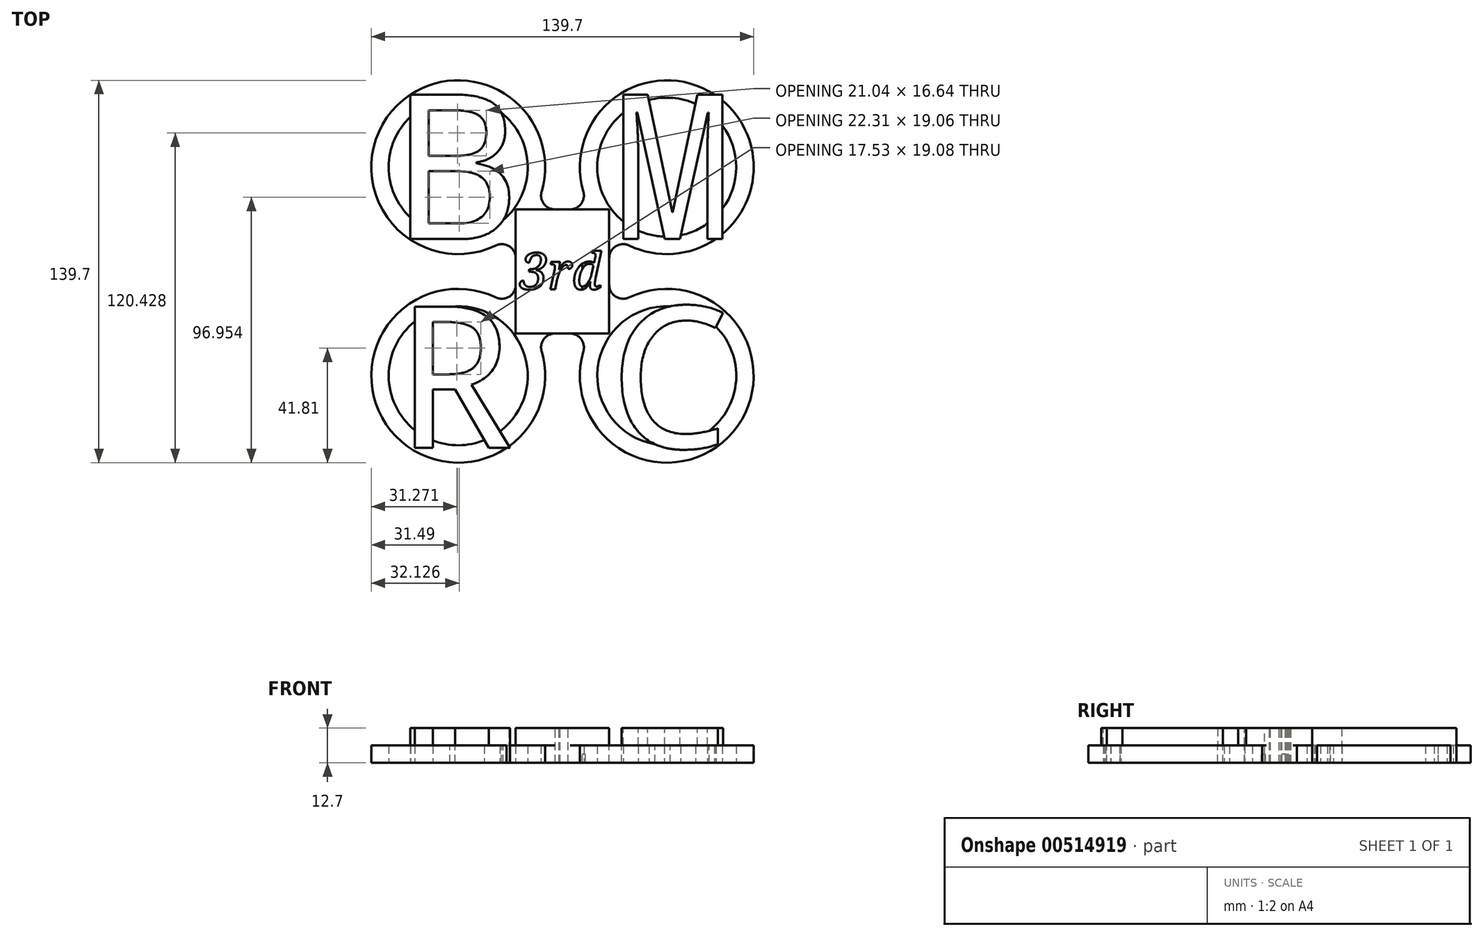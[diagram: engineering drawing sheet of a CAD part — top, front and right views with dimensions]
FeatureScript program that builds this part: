
annotation { "Feature Type Name" : "Feature", "Feature Type Description" : "" }
export const myFeature = defineFeature(function(context is Context, id is Id, definition is map)
    precondition{}
    {
        {
            var Q0;
            Q0=qCreatedBy(makeId("Top.planeOp"),FACE);
            var sketch = newSketch(context, id + "F0", { "sketchPlane" : qUnion([Q0])});
            skLineSegment(sketch, "E0.bottom", {"start": v(38.1, -38.1) * mm, "end": v(-38.1, -38.1) * mm, "construction": true});
            skLineSegment(sketch, "E0.top", {"start": v(38.1, 38.1) * mm, "end": v(-38.1, 38.1) * mm, "construction": true});
            skLineSegment(sketch, "E0.left", {"start": v(38.1, -38.1) * mm, "end": v(38.1, 38.1) * mm, "construction": true});
            skLineSegment(sketch, "E0.right", {"start": v(-38.1, -38.1) * mm, "end": v(-38.1, 38.1) * mm, "construction": true});
            skPoint(sketch, "E0.middle", {"position": v(0, 0) * mm});
            skCircle(sketch, "E1", {"center": v(-38.1, 38.1) * mm, "radius": 31.75 * mm});
            skCircle(sketch, "E2", {"center": v(-38.1, 38.1) * mm, "radius": 25.4 * mm});
            skCircle(sketch, "E3", {"center": v(38.1, 38.1) * mm, "radius": 31.75 * mm});
            skCircle(sketch, "E4", {"center": v(38.1, 38.1) * mm, "radius": 25.4 * mm});
            skCircle(sketch, "E5", {"center": v(-38.1, -38.1) * mm, "radius": 31.75 * mm});
            skCircle(sketch, "E6", {"center": v(-38.1, -38.1) * mm, "radius": 25.4 * mm});
            skCircle(sketch, "E7", {"center": v(38.1, -38.1) * mm, "radius": 31.75 * mm});
            skCircle(sketch, "E8", {"center": v(38.1, -38.1) * mm, "radius": 25.4 * mm});
            skSolve(sketch);
        }
        {
            var Q0;
            Q0=qSketchRegion(id+"F0",true);
            extrude(context, id + "F1", {"entities" : qUnion([Q0]), "depth" : 6.35 * mm, "offsetDistance" : 25.4 * mm});
        }
        {
            var Q0;
            Q0=qCreatedBy(makeId("Top.planeOp"),FACE);
            var sketch = newSketch(context, id + "F2", { "sketchPlane" : qUnion([Q0])});
            skLineSegment(sketch, "E9.bottom", {"start": v(-17.08, -22.68) * mm, "end": v(17.08, -22.68) * mm});
            skLineSegment(sketch, "E9.top", {"start": v(-17.08, 22.68) * mm, "end": v(17.08, 22.68) * mm});
            skLineSegment(sketch, "E9.left", {"start": v(-17.08, -22.68) * mm, "end": v(-17.08, 22.68) * mm});
            skLineSegment(sketch, "E9.right", {"start": v(17.08, -22.68) * mm, "end": v(17.08, 22.68) * mm});
            skPoint(sketch, "E9.middle", {"position": v(0, 0) * mm});
            skSolve(sketch);
        }
        {
            var Q0;
            Q0=qSketchRegion(id+"F2",true);
            extrude(context, id + "F3", {"entities" : qUnion([Q0]), "operationType" : NewBodyOperationType.ADD, "depth" : 12.7 * mm, "offsetDistance" : 25.4 * mm});
        }
        {
            var Q0;
            Q0=makeQuery(id+"F3.opExtrude","CAP_FACE",FACE,{"disambiguationData":[OSD([sQuery(id+"F2.wireOp",EDGE,"E9.bottom"),sQuery(id+"F2.wireOp",EDGE,"E9.top"),sQuery(id+"F2.wireOp",EDGE,"E9.left"),sQuery(id+"F2.wireOp",EDGE,"E9.right")])],"isStart":false});
            var sketch = newSketch(context, id + "F4", { "sketchPlane" : qUnion([Q0])});
            skText(sketch, "E10", { "text": "B", "fontName": "DroidSansMono.ttf"});
            skText(sketch, "E11", { "text": "M", "fontName": "DroidSansMono.ttf"});
            skText(sketch, "E12", { "text": "R", "fontName": "DroidSansMono.ttf"});
            skText(sketch, "E13", { "text": "C", "fontName": "DroidSansMono.ttf"});
            const initialGuessF4  = {"E10": [-0.0605, 0.01187, 1, 0, 0.05322], "E11": [0.01816, 0.01187, 1, 0, 0.05322], "E12": [-0.0605, -0.06445, 1, 0, 0.052], "E13": [0.01708, -0.06445, 1, 0, 0.052]};
            skSetInitialGuess(sketch, initialGuessF4);
            skSolve(sketch);
        }
        {
            var Q0;
            Q0=qSketchRegion(id+"F4",true);
            var Q1;
            Q1=makeQuery(id+"F3.boolean.opBoolean","MERGE",FACE,{"derivedFrom":[makeQuery(id+"F1.opExtrude","CAP_FACE",FACE,{"disambiguationData":[OSD([sQuery(id+"F0.wireOp",EDGE,"E1"),sQuery(id+"F0.wireOp",EDGE,"E2")])],"isStart":true}),makeQuery(id+"F1.opExtrude","CAP_FACE",FACE,{"disambiguationData":[OSD([sQuery(id+"F0.wireOp",EDGE,"E3"),sQuery(id+"F0.wireOp",EDGE,"E4")])],"isStart":true}),makeQuery(id+"F1.opExtrude","CAP_FACE",FACE,{"disambiguationData":[OSD([sQuery(id+"F0.wireOp",EDGE,"E5"),sQuery(id+"F0.wireOp",EDGE,"E6")])],"isStart":true}),makeQuery(id+"F1.opExtrude","CAP_FACE",FACE,{"disambiguationData":[OSD([sQuery(id+"F0.wireOp",EDGE,"E7"),sQuery(id+"F0.wireOp",EDGE,"E8")])],"isStart":true}),makeQuery(id+"F3.opExtrude","CAP_FACE",FACE,{"disambiguationData":[OSD([sQuery(id+"F2.wireOp",EDGE,"E9.bottom"),sQuery(id+"F2.wireOp",EDGE,"E9.top"),sQuery(id+"F2.wireOp",EDGE,"E9.left"),sQuery(id+"F2.wireOp",EDGE,"E9.right")])],"isStart":true})]});
            extrude(context, id + "F5", {"entities" : qUnion([Q0]), "operationType" : NewBodyOperationType.ADD, "endBound" : BoundingType.UP_TO_SURFACE, "oppositeDirection" : true, "depth" : 25.4 * mm, "endBoundEntityFace" : qUnion([Q1]), "offsetDistance" : 25.4 * mm});
        }
        {
            var Q0;
            Q0=makeQuery(id+"F3.opExtrude","CAP_FACE",FACE,{"disambiguationData":[OSD([sQuery(id+"F2.wireOp",EDGE,"E9.bottom"),sQuery(id+"F2.wireOp",EDGE,"E9.top"),sQuery(id+"F2.wireOp",EDGE,"E9.left"),sQuery(id+"F2.wireOp",EDGE,"E9.right")])],"isStart":false});
            var sketch = newSketch(context, id + "F6", { "sketchPlane" : qUnion([Q0])});
            skText(sketch, "E14", { "text": "3rd", "fontName": "NotoSerif-Italic.ttf"});
            const initialGuessF6  = {"E14": [-0.01557, -0.00649, 1, 0, 0.01334]};
            skSetInitialGuess(sketch, initialGuessF6);
            skSolve(sketch);
        }
        {
            var Q0;
            Q0=qSketchRegion(id+"F6",true);
            extrude(context, id + "F7", {"entities" : qUnion([Q0]), "operationType" : NewBodyOperationType.REMOVE, "oppositeDirection" : true, "depth" : 25.4 * mm, "offsetDistance" : 25.4 * mm});
        }
        {
            var Q0;
            {var subQ0=sQuery(id+"F2.wireOp",EDGE,"E9.right");var subQ1=sQuery(id+"F0.wireOp",EDGE,"E8");var subQ2=sQuery(id+"F0.wireOp",EDGE,"E1");var subQ3=sQuery(id+"F0.wireOp",EDGE,"E4");var subQ4=sQuery(id+"F2.wireOp",EDGE,"E9.top");var subQ5=sQuery(id+"F0.wireOp",EDGE,"E2");var subQ6=sQuery(id+"F0.wireOp",EDGE,"E6");var subQ7=sQuery(id+"F2.wireOp",EDGE,"E9.left");var subQ8=sQuery(id+"F0.wireOp",EDGE,"E5");var subQ9=sQuery(id+"F0.wireOp",EDGE,"E7");var subQ10=sQuery(id+"F0.wireOp",EDGE,"E3");var subQ11=sQuery(id+"F2.wireOp",EDGE,"E9.bottom");Q0=makeQuery(id+"F7.boolean.opBoolean","SPLIT",FACE,{"disambiguationData":[TD([makeQuery(id+"F1.opExtrude","SWEPT_FACE",FACE,{"disambiguationData":[OSD([subQ2])]})])],"derivedFrom":makeQuery(id+"F5.boolean.opBoolean","MERGE",FACE,{"derivedFrom":[makeQuery(id+"F3.boolean.opBoolean","MERGE",FACE,{"derivedFrom":[makeQuery(id+"F1.opExtrude","CAP_FACE",FACE,{"disambiguationData":[OSD([subQ2,subQ5])],"isStart":true}),makeQuery(id+"F1.opExtrude","CAP_FACE",FACE,{"disambiguationData":[OSD([subQ10,subQ3])],"isStart":true}),makeQuery(id+"F1.opExtrude","CAP_FACE",FACE,{"disambiguationData":[OSD([subQ8,subQ6])],"isStart":true}),makeQuery(id+"F1.opExtrude","CAP_FACE",FACE,{"disambiguationData":[OSD([subQ9,subQ1])],"isStart":true}),makeQuery(id+"F3.opExtrude","CAP_FACE",FACE,{"disambiguationData":[OSD([subQ11,subQ4,subQ7,subQ0])],"isStart":true})]}),makeQuery(id+"F5.opExtrude","CAP_FACE",FACE,{"disambiguationData":[OSD([subQ2,subQ5,subQ10,subQ3,subQ8,subQ6,subQ9,subQ1,subQ11,subQ4,subQ7,subQ0]),OD(0.0)],"isStart":false}),makeQuery(id+"F5.opExtrude","CAP_FACE",FACE,{"disambiguationData":[OSD([subQ2,subQ5,subQ10,subQ3,subQ8,subQ6,subQ9,subQ1,subQ11,subQ4,subQ7,subQ0]),OD(1.0)],"isStart":false}),makeQuery(id+"F5.opExtrude","CAP_FACE",FACE,{"disambiguationData":[OSD([subQ2,subQ5,subQ10,subQ3,subQ8,subQ6,subQ9,subQ1,subQ11,subQ4,subQ7,subQ0]),OD(2.0)],"isStart":false}),makeQuery(id+"F5.opExtrude","CAP_FACE",FACE,{"disambiguationData":[OSD([subQ2,subQ5,subQ10,subQ3,subQ8,subQ6,subQ9,subQ1,subQ11,subQ4,subQ7,subQ0]),OD(3.0)],"isStart":false})]})});}
            var sketch = newSketch(context, id + "F8", { "sketchPlane" : qUnion([Q0])});
            skLineSegment(sketch, "E15.bottom", {"start": v(7.21, 7.52) * mm, "end": v(8.42, 7.52) * mm});
            skLineSegment(sketch, "E15.top", {"start": v(7.21, 3.8) * mm, "end": v(8.42, 3.8) * mm});
            skLineSegment(sketch, "E15.left", {"start": v(7.21, 7.52) * mm, "end": v(7.21, 3.8) * mm});
            skLineSegment(sketch, "E15.right", {"start": v(8.42, 7.52) * mm, "end": v(8.42, 3.8) * mm});
            skLineSegment(sketch, "E16.bottom", {"start": v(7.21, -0.48) * mm, "end": v(8.42, -0.48) * mm});
            skLineSegment(sketch, "E16.top", {"start": v(7.21, -4.67) * mm, "end": v(8.42, -4.67) * mm});
            skLineSegment(sketch, "E16.left", {"start": v(7.21, -0.48) * mm, "end": v(7.21, -4.67) * mm});
            skLineSegment(sketch, "E16.right", {"start": v(8.42, -0.48) * mm, "end": v(8.42, -4.67) * mm});
            skSolve(sketch);
        }
        {
            var Q0;
            Q0 = qSketchRegion(id + "F8", true);
            extrude(context, id + "F9", {"entities" : qUnion([Q0]), "operationType" : NewBodyOperationType.ADD, "oppositeDirection" : true, "depth" : 3.17 * mm, "offsetDistance" : 25.4 * mm});
        }
        {
            var Q0;
            Q0=makeQuery(id+"F3.boolean.opBoolean","INTERSECT",EDGE,{"derivedFrom":[makeQuery(id+"F1.opExtrude","SWEPT_FACE",FACE,{"disambiguationData":[OSD([sQuery(id+"F0.wireOp",EDGE,"E7")])]}),makeQuery(id+"F3.opExtrude","SWEPT_FACE",FACE,{"disambiguationData":[OSD([sQuery(id+"F2.wireOp",EDGE,"E9.right")])]})]});
            var Q1;
            Q1=makeQuery(id+"F3.boolean.opBoolean","INTERSECT",EDGE,{"derivedFrom":[makeQuery(id+"F1.opExtrude","SWEPT_FACE",FACE,{"disambiguationData":[OSD([sQuery(id+"F0.wireOp",EDGE,"E3")])]}),makeQuery(id+"F3.opExtrude","SWEPT_FACE",FACE,{"disambiguationData":[OSD([sQuery(id+"F2.wireOp",EDGE,"E9.right")])]})]});
            var Q2;
            Q2=makeQuery(id+"F3.boolean.opBoolean","INTERSECT",EDGE,{"derivedFrom":[makeQuery(id+"F1.opExtrude","SWEPT_FACE",FACE,{"disambiguationData":[OSD([sQuery(id+"F0.wireOp",EDGE,"E3")])]}),makeQuery(id+"F3.opExtrude","SWEPT_FACE",FACE,{"disambiguationData":[OSD([sQuery(id+"F2.wireOp",EDGE,"E9.top")])]})]});
            var Q3;
            Q3=makeQuery(id+"F3.boolean.opBoolean","INTERSECT",EDGE,{"derivedFrom":[makeQuery(id+"F1.opExtrude","SWEPT_FACE",FACE,{"disambiguationData":[OSD([sQuery(id+"F0.wireOp",EDGE,"E1")])]}),makeQuery(id+"F3.opExtrude","SWEPT_FACE",FACE,{"disambiguationData":[OSD([sQuery(id+"F2.wireOp",EDGE,"E9.top")])]})]});
            var Q4;
            Q4=makeQuery(id+"F3.boolean.opBoolean","INTERSECT",EDGE,{"derivedFrom":[makeQuery(id+"F1.opExtrude","SWEPT_FACE",FACE,{"disambiguationData":[OSD([sQuery(id+"F0.wireOp",EDGE,"E1")])]}),makeQuery(id+"F3.opExtrude","SWEPT_FACE",FACE,{"disambiguationData":[OSD([sQuery(id+"F2.wireOp",EDGE,"E9.left")])]})]});
            var Q5;
            Q5=makeQuery(id+"F3.boolean.opBoolean","INTERSECT",EDGE,{"derivedFrom":[makeQuery(id+"F1.opExtrude","SWEPT_FACE",FACE,{"disambiguationData":[OSD([sQuery(id+"F0.wireOp",EDGE,"E5")])]}),makeQuery(id+"F3.opExtrude","SWEPT_FACE",FACE,{"disambiguationData":[OSD([sQuery(id+"F2.wireOp",EDGE,"E9.left")])]})]});
            var Q6;
            Q6=makeQuery(id+"F3.boolean.opBoolean","INTERSECT",EDGE,{"derivedFrom":[makeQuery(id+"F1.opExtrude","SWEPT_FACE",FACE,{"disambiguationData":[OSD([sQuery(id+"F0.wireOp",EDGE,"E7")])]}),makeQuery(id+"F3.opExtrude","SWEPT_FACE",FACE,{"disambiguationData":[OSD([sQuery(id+"F2.wireOp",EDGE,"E9.bottom")])]})]});
            var Q7;
            Q7=makeQuery(id+"F3.boolean.opBoolean","INTERSECT",EDGE,{"derivedFrom":[makeQuery(id+"F1.opExtrude","SWEPT_FACE",FACE,{"disambiguationData":[OSD([sQuery(id+"F0.wireOp",EDGE,"E5")])]}),makeQuery(id+"F3.opExtrude","SWEPT_FACE",FACE,{"disambiguationData":[OSD([sQuery(id+"F2.wireOp",EDGE,"E9.bottom")])]})]});
            fillet(context, id + "F10", {"entities" : qUnion([Q0, Q1, Q2, Q3, Q4, Q5, Q6, Q7]), "radius" : 5.08 * mm, "tangentPropagation" : true, "allowEdgeOverflow" : false});
        }
    });
